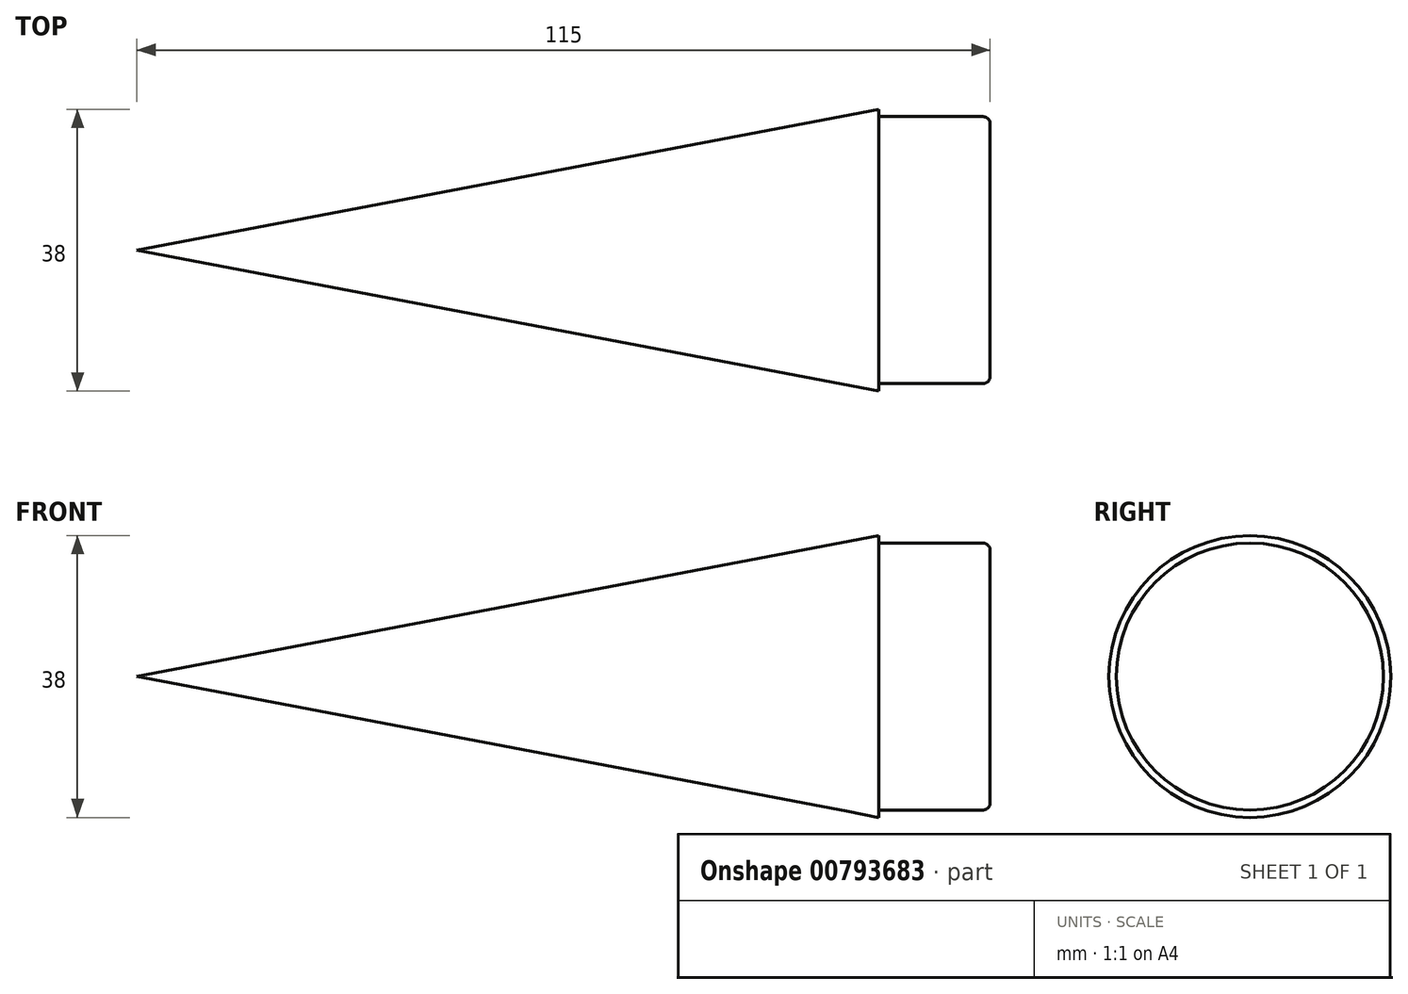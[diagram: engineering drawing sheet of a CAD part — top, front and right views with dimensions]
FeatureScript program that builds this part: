
annotation { "Feature Type Name" : "Feature", "Feature Type Description" : "" }
export const myFeature = defineFeature(function(context is Context, id is Id, definition is map)
    precondition{}
    {
        {
            var Q0;
            Q0=qCreatedBy(makeId("Top.planeOp"),FACE);
            var sketch = newSketch(context, id + "F0", { "sketchPlane" : qUnion([Q0])});
            skLineSegment(sketch, "E0", {"start": v(100, 0) * mm, "end": v(-49.92, 0) * mm, "construction": true});
            skLineSegment(sketch, "E1", {"start": v(0, 0) * mm, "end": v(0, 19) * mm, "construction": true});
            skLineSegment(sketch, "E2", {"start": v(100, 0) * mm, "end": v(100, 19) * mm, "construction": true});
            skLineSegment(sketch, "E3", {"start": v(-37.94, 19) * mm, "end": v(100, 19) * mm, "construction": true});
            skLineSegment(sketch, "E4.bottom", {"start": v(100, 18) * mm, "end": v(114, 18) * mm});
            skLineSegment(sketch, "E4.right", {"start": v(115, 17) * mm, "end": v(115, 0) * mm});
            skLineSegment(sketch, "E5", {"start": v(100, 19) * mm, "end": v(100, 18) * mm});
            skLineSegment(sketch, "E6", {"start": v(0, 0) * mm, "end": v(115, 0) * mm});
            skLineSegment(sketch, "E7.left", {"start": v(100, 19) * mm, "end": v(100, 19) * mm});
            skLineSegment(sketch, "E8.left", {"start": v(0, 0) * mm, "end": v(0, 14.5) * mm});
            skPoint(sketch, "E9.visualSharp", {"position": v(115, 18) * mm});
            skArc(sketch, "E9.filletArc", {"start": v(115, 17) * mm, "mid": v(114.7, 17.7) * mm, "end": v(114, 18) * mm});
            skSolve(sketch);
        }
        {
            var Q0;
            Q0=qCreatedBy(makeId("Top.planeOp"),FACE);
            var sketch = newSketch(context, id + "F1", { "sketchPlane" : qUnion([Q0])});
            skLineSegment(sketch, "E10.0", {"start": v(100, 0) * mm, "end": v(-49.92, 0) * mm});
            skLineSegment(sketch, "E10.1", {"start": v(0, 0) * mm, "end": v(0, 19) * mm});
            skLineSegment(sketch, "E10.2", {"start": v(100, 0) * mm, "end": v(100, 19) * mm});
            skLineSegment(sketch, "E10.4", {"start": v(100, 18) * mm, "end": v(114, 18) * mm});
            skLineSegment(sketch, "E10.5", {"start": v(115, 17) * mm, "end": v(115, 0) * mm});
            skLineSegment(sketch, "E10.6", {"start": v(100, 19) * mm, "end": v(100, 18) * mm});
            skLineSegment(sketch, "E10.7", {"start": v(0, 0) * mm, "end": v(115, 0) * mm});
            skPoint(sketch, "E10.8", {"position": v(100, 19) * mm});
            skLineSegment(sketch, "E10.9", {"start": v(0, 0) * mm, "end": v(115, 0) * mm});
            skLineSegment(sketch, "E10.10", {"start": v(0, 0) * mm, "end": v(0, 14.5) * mm});
            skPoint(sketch, "E11.11", {"position": v(115, 18) * mm});
            skArc(sketch, "E11.12", {"start": v(115, 17) * mm, "mid": v(114.7, 17.7) * mm, "end": v(114, 18) * mm});
            skLineSegment(sketch, "E12", {"start": v(0, 0) * mm, "end": v(100, 19) * mm});
            skSolve(sketch);
        }
        {
            var Q0;
            Q0 = qSketchRegion(id + "F1", true);
            var Q1;
            Q1=sQuery(id+"F1.wireOp",EDGE,"E10.9");
            revolve(context, id + "F2", {"surfaceOperationType" : NewSurfaceOperationType.NEW, "entities" : qUnion([Q0]), "axis" : qUnion([Q1]), "revolveType" : RevolveType.FULL});
        }
    });
